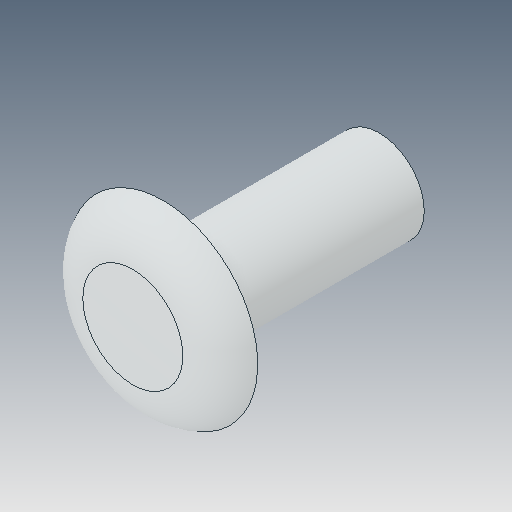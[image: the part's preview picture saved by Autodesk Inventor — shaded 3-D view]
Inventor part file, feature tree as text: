
AUTODESK INVENTOR PART (.ipt)
format: ipt  version: 2023.5 (Build 275446000, 446)  size: 107,520 bytes
history: native  units: in
note: dims shown in document units (in); Inventor stores cm internally (conversion verified against a paired STEP export)
features: fillet x1
ambient origin geometry x8: Origin, YZ Plane, XZ Plane, XY Plane, X Axis, Y Axis, Z Axis, Center Point
bodies: Solid1 (feature_tree)
feature tree (1):
  fillet  "Fillet1"  [1 undecoded]
note: 1 required parameter value undecoded (feature->parameter linkage not recoverable at this tier; creation-order binding heuristic only, values carry confidence <= 0.55)
